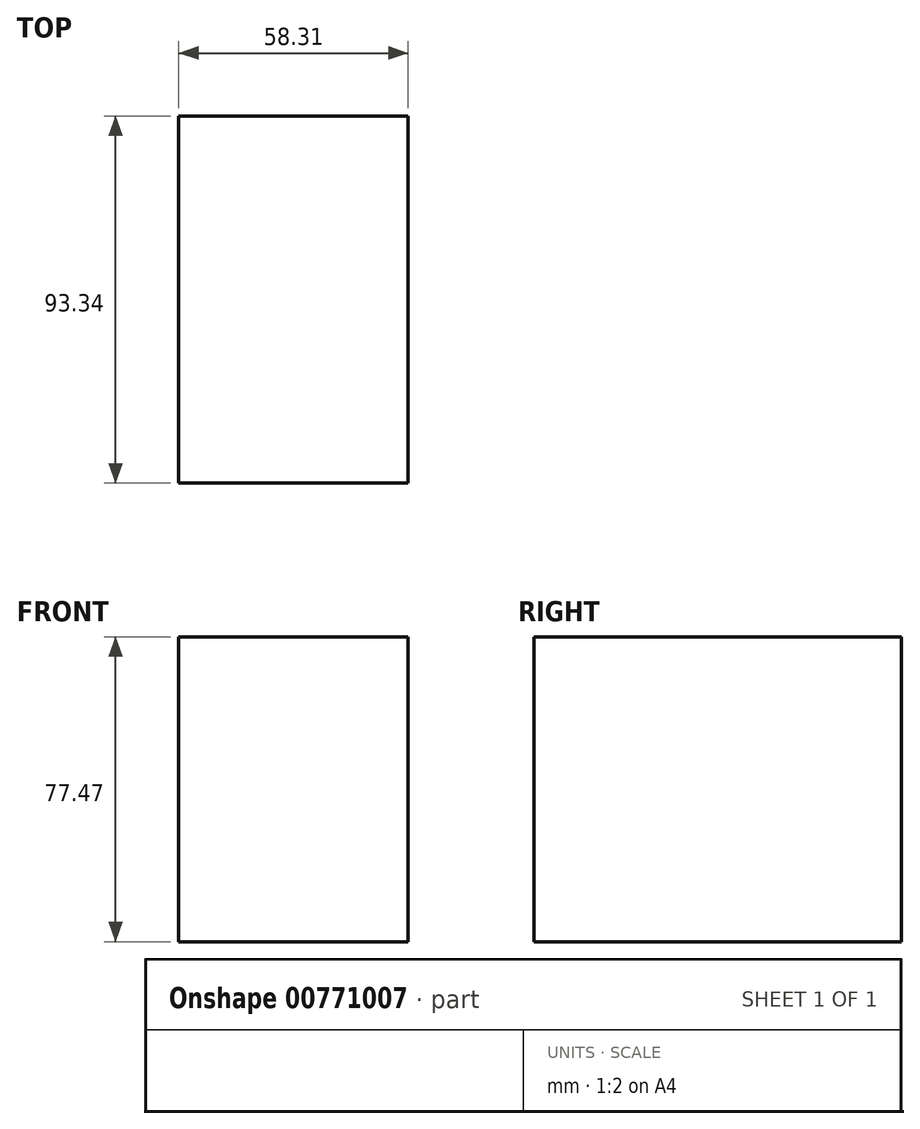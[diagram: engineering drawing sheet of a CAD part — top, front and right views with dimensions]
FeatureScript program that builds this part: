
annotation { "Feature Type Name" : "Feature", "Feature Type Description" : "" }
export const myFeature = defineFeature(function(context is Context, id is Id, definition is map)
    precondition{}
    {
        {
            var Q0;
            Q0=qCreatedBy(makeId("Top.planeOp"),FACE);
            var sketch = newSketch(context, id + "F0", { "sketchPlane" : qUnion([Q0])});
            skLineSegment(sketch, "E0.bottom", {"start": v(-8.14, 46.5) * mm, "end": v(50.17, 46.5) * mm});
            skLineSegment(sketch, "E0.top", {"start": v(-8.14, -46.83) * mm, "end": v(50.17, -46.83) * mm});
            skLineSegment(sketch, "E0.left", {"start": v(-8.14, 46.5) * mm, "end": v(-8.14, -46.83) * mm});
            skLineSegment(sketch, "E0.right", {"start": v(50.17, 46.5) * mm, "end": v(50.17, -46.83) * mm});
            skLineSegment(sketch, "E1.bottom", {"start": v(-40.52, -16.37) * mm, "end": v(-31.76, -16.37) * mm});
            skLineSegment(sketch, "E1.top", {"start": v(-40.52, -42.76) * mm, "end": v(-31.76, -42.76) * mm});
            skLineSegment(sketch, "E1.left", {"start": v(-40.52, -16.37) * mm, "end": v(-40.52, -42.76) * mm});
            skLineSegment(sketch, "E1.right", {"start": v(-31.76, -16.37) * mm, "end": v(-31.76, -42.76) * mm});
            skSolve(sketch);
        }
        {
            var Q0;
            Q0=makeQuery(id+"F0.imprint","IMPRINT",FACE,{"disambiguationData":[TD([[makeQuery(id+"F0.imprint","IMPRINT",EDGE,{"derivedFrom":sQuery(id+"F0.wireOp",EDGE,"E0.bottom")}),-1.0]])]});
            extrude(context, id + "F1", {"entities" : qUnion([Q0]), "depth" : 77.47 * mm, "offsetDistance" : 25.4 * mm});
        }
    });
